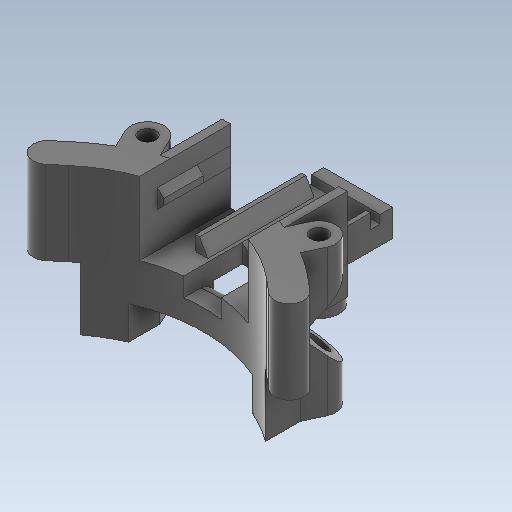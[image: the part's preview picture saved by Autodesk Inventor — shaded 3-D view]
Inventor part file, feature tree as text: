
AUTODESK INVENTOR PART (.ipt)
format: ipt  version: 2020 (Build 240168000, 168)  size: 793,088 bytes
history: native  units: mm
features: extrude x18, sketch x17, projected_geometry x15, other x5, chamfer x2, sweep x1, fillet x1
ambient origin geometry x8: Origin, YZ Plane, XZ Plane, XY Plane, X Axis, Y Axis, Z Axis, Center Point
bodies: Body1 (feature_tree)
feature tree (59):
  other  "Твердое тело1"
  extrude  "Выдавливание1"  Depth=35.0mm TaperAngle=0.0deg
  sketch  "Эскиз2"
  extrude  "Выдавливание2"  Depth=4.0mm
  sweep  "Сдвиг1"
  extrude  "Выдавливание5"  Depth=8.0mm
  extrude  "Выдавливание6"  Depth=35.0mm TaperAngle=0.0deg
  extrude  "Выдавливание7"  Depth=8.5mm
  extrude  "Выдавливание8"  TaperAngle=45.0deg  [1 undecoded]
  other  "РабПлоскость1"
  extrude  "Выдавливание9"  Depth=8.5mm
  extrude  "Выдавливание10"  TaperAngle=45.0deg  [1 undecoded]
  extrude  "Выдавливание11"  TaperAngle=0.0deg  [1 undecoded]
  sketch  "Эскиз13"
  other  "РабПлоскость2"
  sketch  "Эскиз14"
  extrude  "Выдавливание12"  Depth=5.0mm TaperAngle=0.0deg
  extrude  "Выдавливание13"  Depth=15.0mm TaperAngle=0.0deg
  other  "РабПлоскость3"
  extrude  "Выдавливание14"  Depth=15.0mm TaperAngle=0.0deg
  extrude  "Выдавливание15"  Depth=26.0mm
  extrude  "Выдавливание16"  Depth=6.0mm
  extrude  "Выдавливание17"  Depth=15.0mm TaperAngle=0.0deg
  chamfer  "Фаска1"  Distance=2.0mm
  other  "РабПлоскость4"
  sketch  "Эскиз18"
  extrude  "Выдавливание18"  Depth=1.5mm
  extrude  "Выдавливание19"  Depth=3.0mm
  extrude  "Выдавливание20"  Depth=6.0mm
  chamfer  "Фаска2"  Distance=2.5mm
  fillet  "Сопряжение1"  [1 undecoded]
  sketch  "Эскиз1"
  sketch  "Эскиз3"
  projected_geometry  "Спроецированная петля1"
  projected_geometry  "Спроецированная петля2"
  sketch  "3D эскиз1"
  sketch  "Эскиз4"
  sketch  "Эскиз6"
  projected_geometry  "Спроецированная петля4"
  sketch  "Эскиз7"
  projected_geometry  "Спроецированная петля5"
  sketch  "Эскиз9"
  projected_geometry  "Спроецированная петля7"
  sketch  "Эскиз11"
  projected_geometry  "Спроецированная петля8"
  sketch  "Эскиз12"
  projected_geometry  "Спроецированная петля9"
  projected_geometry  "Спроецированная петля10"
  sketch  "Эскиз15"
  sketch  "Эскиз16"
  projected_geometry  "Спроецированная петля11"
  projected_geometry  "Спроецированная петля12"
  sketch  "Эскиз17"
  projected_geometry  "Спроецированная петля13"
  projected_geometry  "Спроецированная петля14"
  projected_geometry  "Спроецированная петля15"
  projected_geometry  "Спроецированная петля16"
  sketch  "Эскиз19"
  projected_geometry  "Спроецированная петля17"
note: 4 required parameter values undecoded (feature->parameter linkage not recoverable at this tier; creation-order binding heuristic only, values carry confidence <= 0.55)
